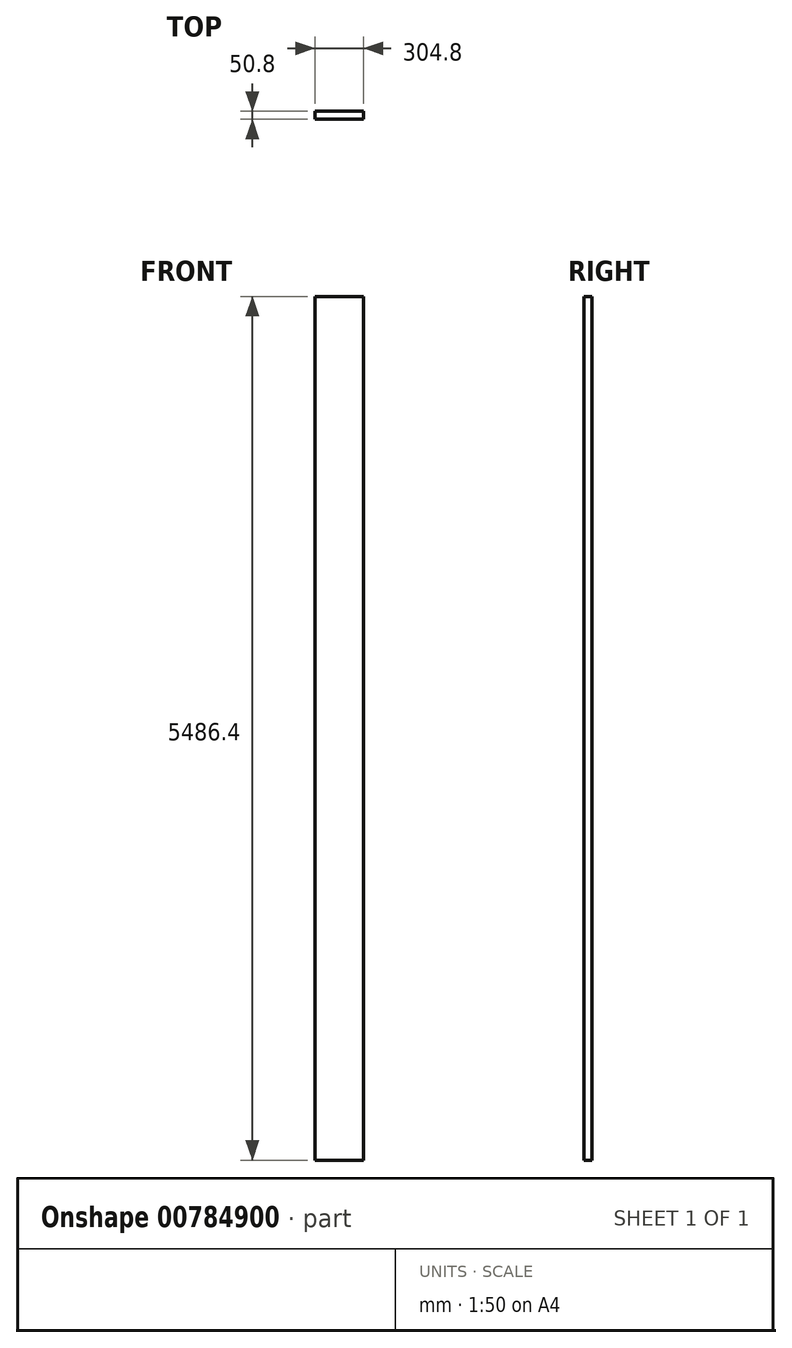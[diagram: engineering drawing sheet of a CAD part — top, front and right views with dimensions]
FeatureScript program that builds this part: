
annotation { "Feature Type Name" : "Feature", "Feature Type Description" : "" }
export const myFeature = defineFeature(function(context is Context, id is Id, definition is map)
    precondition{}
    {
        {
            var Q0;
            Q0=qCreatedBy(makeId("Front.planeOp"),FACE);
            var sketch = newSketch(context, id + "F0", { "sketchPlane" : qUnion([Q0])});
            skLineSegment(sketch, "E0.bottom", {"start": v(152.4, 2743.2) * mm, "end": v(-152.4, 2743.2) * mm});
            skLineSegment(sketch, "E0.top", {"start": v(152.4, -2743.2) * mm, "end": v(-152.4, -2743.2) * mm});
            skLineSegment(sketch, "E0.left", {"start": v(152.4, 2743.2) * mm, "end": v(152.4, -2743.2) * mm});
            skLineSegment(sketch, "E0.right", {"start": v(-152.4, 2743.2) * mm, "end": v(-152.4, -2743.2) * mm});
            skPoint(sketch, "E0.middle", {"position": v(0, 0) * mm});
            skSolve(sketch);
        }
        {
            var Q0;
            Q0=makeQuery(id+"F0.imprint","IMPRINT",FACE,{"disambiguationData":[TD([[makeQuery(id+"F0.imprint","IMPRINT",EDGE,{"derivedFrom":sQuery(id+"F0.wireOp",EDGE,"E0.bottom")}),1.0]])]});
            extrude(context, id + "F1", {"entities" : qUnion([Q0]), "depth" : 50.8 * mm, "offsetDistance" : 25.4 * mm});
        }
    });
